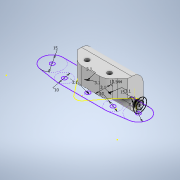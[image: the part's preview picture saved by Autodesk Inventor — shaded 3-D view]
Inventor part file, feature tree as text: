
AUTODESK INVENTOR PART (.ipt)
format: ipt  version: 2020 (Build 240168000, 168)  size: 282,624 bytes
history: native  units: in
note: dims shown in document units (in); Inventor stores cm internally (conversion verified against a paired STEP export)
features: extrude x10, sketch x9, fillet x4, projected_geometry x2
ambient origin geometry x8: Origin, YZ Plane, XZ Plane, XY Plane, X Axis, Y Axis, Z Axis, Center Point
bodies: Solid1 (feature_tree)
feature tree (25):
  sketch  "Sketch1"  dims[d0=0.3937in d1=0.3937in d2=0.5906in d3=0.5906in d4=0.122in d5=0.122in d6=0.122in d7=0.2362in d8=0.0in]
  sketch  "Sketch2"  dims[d9=0.3346in d10=0.0in d11=0.2953in]
  sketch  "Sketch3"  dims[d12=0.2756in d13=0.0in d15=0.2346in d16=0.1543in]
  extrude  "Extrusion1"  Depth=0.3937in TaperAngle=0.0deg
  extrude  "Extrusion2"  Depth=0.2953in
  extrude  "Extrusion3"  Depth=0.2346in
  sketch  "Sketch6"  dims[d23=0.3346in d24=0.0in d25=0.1181in]
  fillet  "Fillet2"  Radius=0.1543in
  extrude  "Extrusion4"  Depth=0.3543in
  extrude  "Extrusion5"  Depth=0.0394in
  fillet  "Fillet3"  Radius=0.3346in
  extrude  "Extrusion6"  Depth=0.1181in
  extrude  "Extrusion7"  Depth=0.315in TaperAngle=0.0deg
  fillet  "Fillet4"  Radius=0.315in
  extrude  "Extrusion8"  Depth=1.378in
  extrude  "Extrusion9"  Depth=0.315in
  fillet  "Fillet5"  Radius=0.122in
  extrude  "Extrusion10"  Depth=0.315in
  sketch  "Sketch4"  dims[d17=0.2008in d18=0.3543in]
  projected_geometry  "Projected Loop1"
  sketch  "Sketch5"  dims[d19=0.0394in d20=0.0394in d21=0.3346in d22=0.0in]
  sketch  "Sketch7"  dims[d26=0.3346in d27=0.0in d28=0.2362in d29=0.0in d30=0.315in]
  projected_geometry  "Projected Loop2"
  sketch  "Sketch8"  dims[d32=0.0in d33=0.0in d34=1.378in]
  sketch  "Sketch9"  dims[d35=0.2362in d36=0.0in d37=0.315in d38=0.122in d39=0.122in d40=0.2362in d41=0.0in d42=0.4151in]
